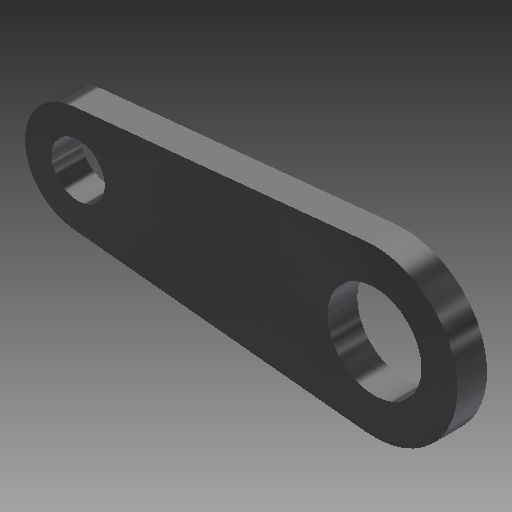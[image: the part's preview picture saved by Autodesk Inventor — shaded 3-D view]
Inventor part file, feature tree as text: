
AUTODESK INVENTOR PART (.ipt)
format: ipt  version: 2019 (Build 230136000, 136)  size: 136,192 bytes
history: native  units: mm
features: other x4, sketch x3, hole x2, extrude x1
ambient origin geometry x8: Origin, YZ Plane, XZ Plane, XY Plane, X Axis, Y Axis, Z Axis, Center Point
bodies: Solid1 (feature_tree)
feature tree (10):
  extrude  "Extrusion1"  Depth=28.0mm
  hole  "Hole1"  [1 undecoded]
  hole  "Hole2"  [1 undecoded]
  other  "Work Point1"
  other  "Work Point2"
  sketch  "Sketch1"  dims[d0=18.0mm d1=28.0mm]
  sketch  "Sketch2"  dims[d2=50.0mm d3=5.0mm d4=0.0mm]
  sketch  "Sketch3"  dims[d5=15.84mm d6=6.0mm d7=4.0mm d8=2.0mm d9=90.0deg d10=8.0mm d11=20.594885mm d12=9.0mm d13=6.0mm d14=4.0mm d15=2.0mm d16=90.0deg d17=8.0mm d18=20.594885mm d33=0.0mm d34=-89714.6mm d35=0.0mm d36=0.0mm d37=89714.6mm d38=3415340.0mm d39=-203486.0mm d40=682943.0mm d41=0.0mm d42=203062.0mm d43=-683232.0mm d44=0.0mm d45=9810.0mm d46=1.624727mm]
  other  "Work Axis1"
  other  "Work Axis2"
note: 2 required parameter values undecoded (feature->parameter linkage not recoverable at this tier; creation-order binding heuristic only, values carry confidence <= 0.55)
